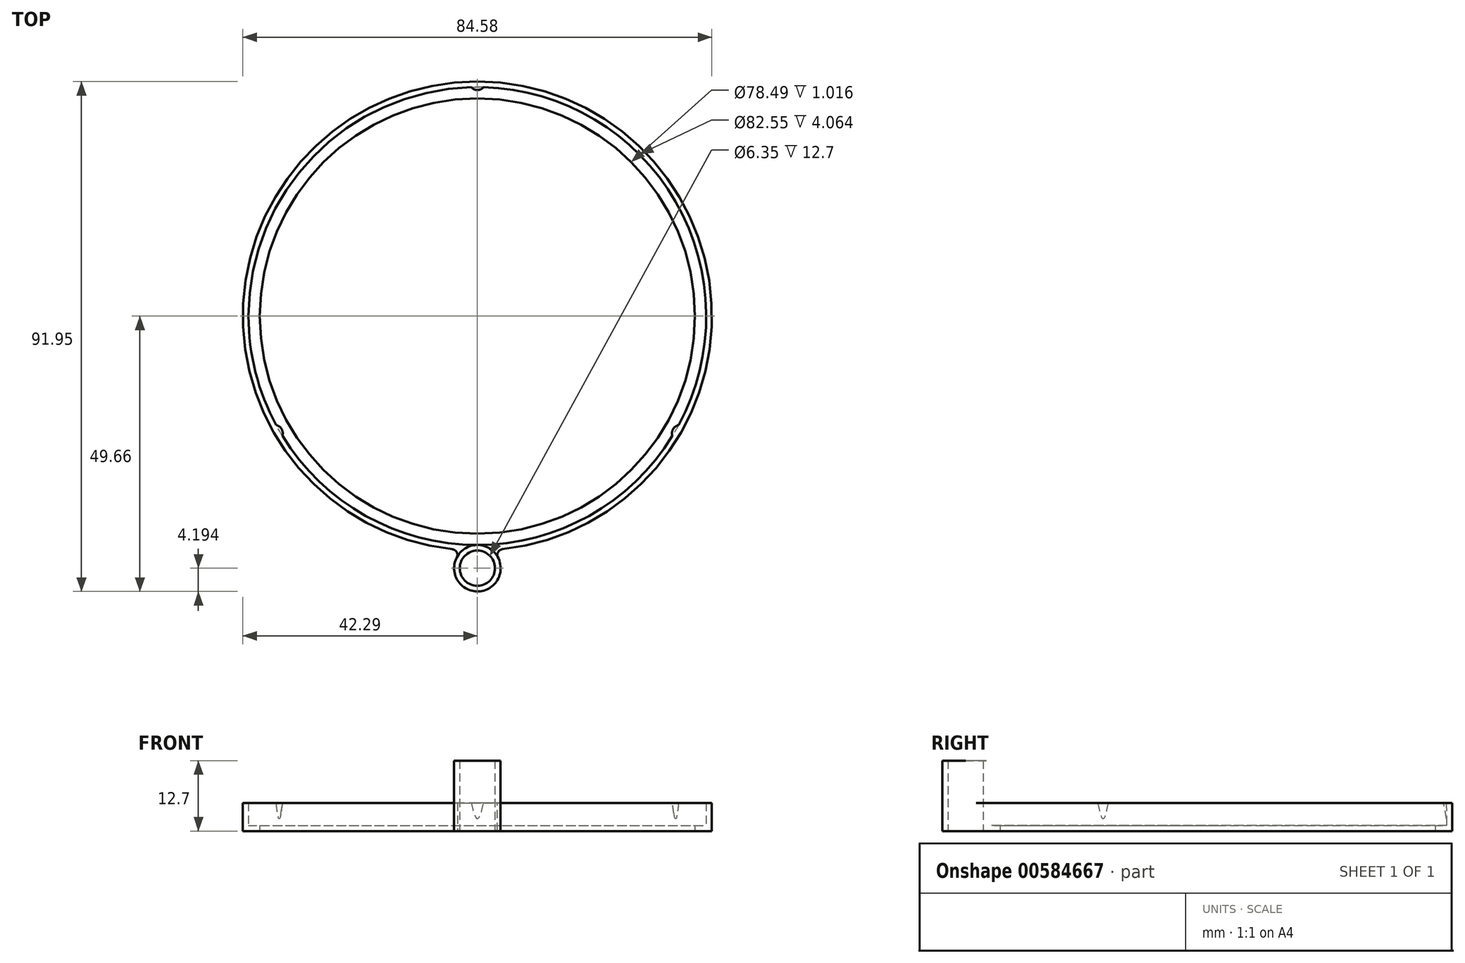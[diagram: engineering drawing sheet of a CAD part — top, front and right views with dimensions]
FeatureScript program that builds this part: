
annotation { "Feature Type Name" : "Feature", "Feature Type Description" : "" }
export const myFeature = defineFeature(function(context is Context, id is Id, definition is map)
    precondition{}
    {
        {
            var Q0;
            Q0=qCreatedBy(makeId("Front.planeOp"),FACE);
            var sketch = newSketch(context, id + "F0", { "sketchPlane" : qUnion([Q0])});
            skLineSegment(sketch, "E0", {"start": v(39.24, 0) * mm, "end": v(42.3, 0) * mm});
            skLineSegment(sketch, "E1", {"start": v(42.3, 0) * mm, "end": v(42.3, 5.08) * mm});
            skLineSegment(sketch, "E2", {"start": v(42.3, 5.08) * mm, "end": v(41.28, 5.08) * mm});
            skLineSegment(sketch, "E3", {"start": v(41.28, 5.08) * mm, "end": v(41.28, 1.02) * mm});
            skLineSegment(sketch, "E4", {"start": v(41.28, 1.02) * mm, "end": v(39.24, 1.02) * mm});
            skLineSegment(sketch, "E5", {"start": v(39.24, 1.02) * mm, "end": v(39.24, 0) * mm});
            skLineSegment(sketch, "E6", {"start": v(0, 0) * mm, "end": v(0, 6.3) * mm, "construction": true});
            skSolve(sketch);
        }
        {
            var Q0;
            Q0 = qSketchRegion(id + "F0", true);
            var Q1;
            Q1=sQuery(id+"F0.wireOp",EDGE,"E6");
            revolve(context, id + "F1", {"entities" : qUnion([Q0]), "axis" : qUnion([Q1]), "revolveType" : RevolveType.FULL});
        }
        {
            var Q0;
            Q0=qCreatedBy(makeId("Top.planeOp"),FACE);
            var sketch = newSketch(context, id + "F2", { "sketchPlane" : qUnion([Q0])});
            skCircle(sketch, "E7", {"center": v(0, -45.47) * mm, "radius": 3.18 * mm});
            skCircle(sketch, "E8", {"center": v(0, -45.47) * mm, "radius": 4.2 * mm});
            skSolve(sketch);
        }
        {
            var Q0;
            Q0 = qSketchRegion(id + "F2", true);
            extrude(context, id + "F3", {"entities" : qUnion([Q0]), "operationType" : NewBodyOperationType.ADD, "depth" : 12.7 * mm, "offsetDistance" : 25.4 * mm});
        }
        {
            var Q0;
            Q0=makeQuery(id+"F3.boolean.opBoolean","INTERSECT",EDGE,{"disambiguationData":[OD(0.0)],"derivedFrom":[makeQuery(id+"F1.opRevolve","SWEPT_FACE",FACE,{"disambiguationData":[OSD([sQuery(id+"F0.wireOp",EDGE,"E1")])]}),makeQuery(id+"F3.opExtrude","SWEPT_FACE",FACE,{"disambiguationData":[OSD([sQuery(id+"F2.wireOp",EDGE,"E8")])]})]});
            var Q1;
            Q1=makeQuery(id+"F3.boolean.opBoolean","INTERSECT",EDGE,{"disambiguationData":[OD(1.0)],"derivedFrom":[makeQuery(id+"F1.opRevolve","SWEPT_FACE",FACE,{"disambiguationData":[OSD([sQuery(id+"F0.wireOp",EDGE,"E1")])]}),makeQuery(id+"F3.opExtrude","SWEPT_FACE",FACE,{"disambiguationData":[OSD([sQuery(id+"F2.wireOp",EDGE,"E8")])]})]});
            fillet(context, id + "F4", {"entities" : qUnion([Q0, Q1]), "radius" : 1.02 * mm, "tangentPropagation" : true, "allowEdgeOverflow" : false});
        }
        {
            var Q0;
            Q0=makeQuery(id+"F1.opRevolve","SWEPT_FACE",FACE,{"disambiguationData":[OSD([sQuery(id+"F0.wireOp",EDGE,"E2")])]});
            var sketch = newSketch(context, id + "F5", { "sketchPlane" : qUnion([Q0])});
            skArc(sketch, "E9", {"start": v(-1.52, 42.26) * mm, "mid": v(0, 40.77) * mm, "end": v(1.52, 42.26) * mm});
            skArc(sketch, "E10", {"start": v(1.52, 42.26) * mm, "mid": v(0, 42.3) * mm, "end": v(-1.52, 42.26) * mm});
            skArc(sketch, "E11", {"start": v(-35.84, -22.45) * mm, "mid": v(-35.3, -20.38) * mm, "end": v(-37.36, -19.81) * mm});
            skArc(sketch, "E12", {"start": v(37.36, -19.81) * mm, "mid": v(35.3, -20.38) * mm, "end": v(35.84, -22.45) * mm});
            skLineSegment(sketch, "E13", {"start": v(0, 0) * mm, "end": v(-36.63, -21.15) * mm, "construction": true});
            skLineSegment(sketch, "E14", {"start": v(0, 0) * mm, "end": v(36.63, -21.15) * mm, "construction": true});
            skArc(sketch, "E15", {"start": v(-37.36, -19.81) * mm, "mid": v(-36.63, -21.15) * mm, "end": v(-35.84, -22.45) * mm});
            skArc(sketch, "E16.trimOffspring", {"start": v(35.84, -22.45) * mm, "mid": v(36.63, -21.15) * mm, "end": v(37.36, -19.81) * mm});
            skSolve(sketch);
        }
        {
            var Q0;
            Q0 = qSketchRegion(id + "F5", true);
            extrude(context, id + "F6", {"entities" : qUnion([Q0]), "operationType" : NewBodyOperationType.ADD, "oppositeDirection" : true, "depth" : 3.05 * mm, "offsetDistance" : 25.4 * mm, "hasDraft" : true, "draftAngle" : 10 * degree, "draftPullDirection" : true});
        }
    });
